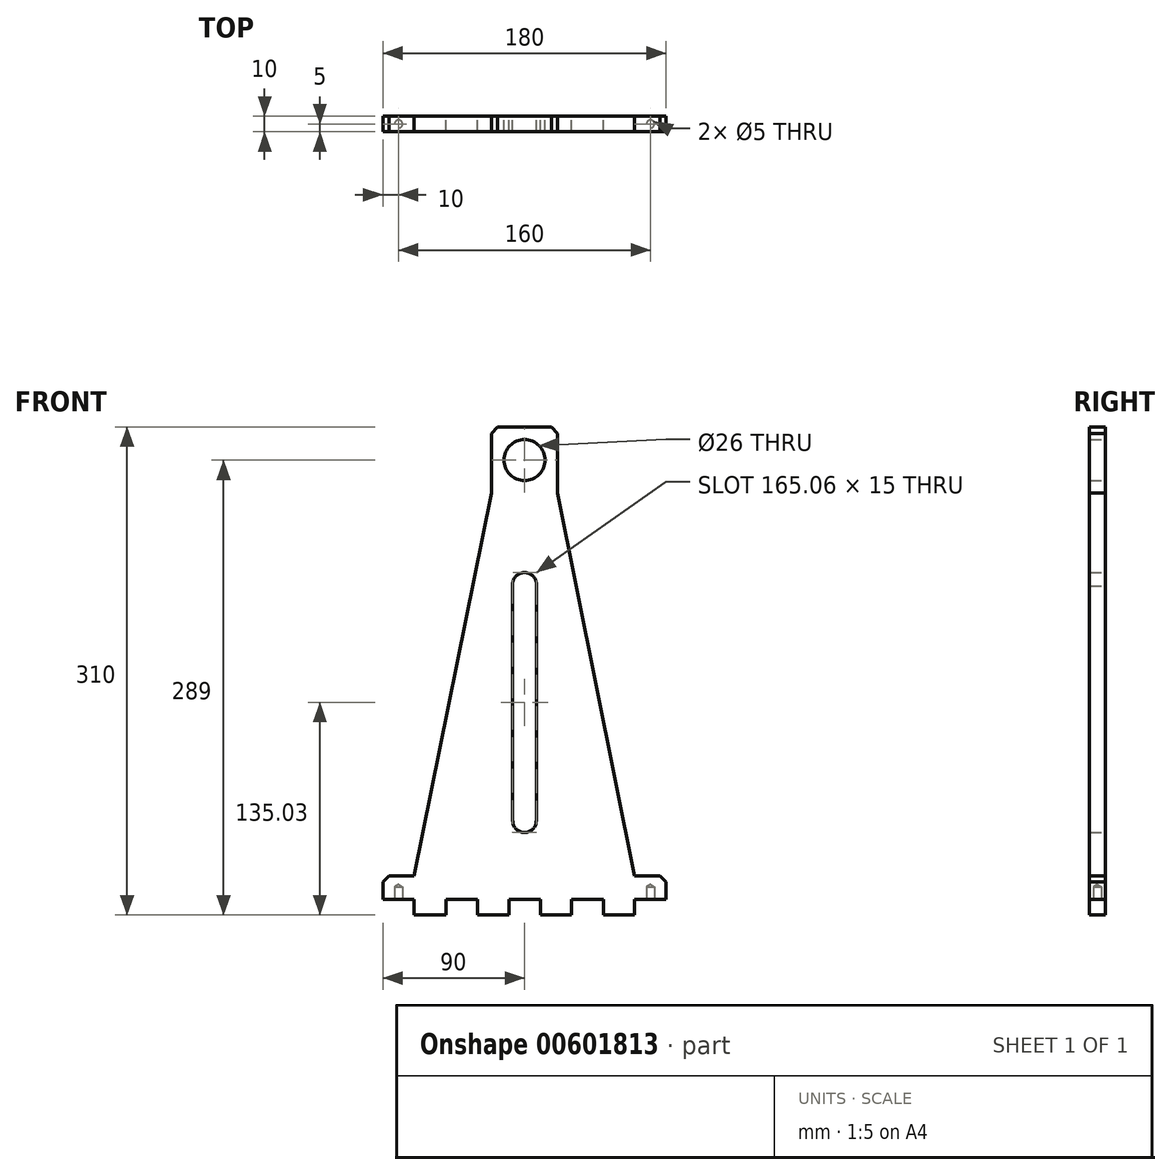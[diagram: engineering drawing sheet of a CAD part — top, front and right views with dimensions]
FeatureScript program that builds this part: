
annotation { "Feature Type Name" : "Feature", "Feature Type Description" : "" }
export const myFeature = defineFeature(function(context is Context, id is Id, definition is map)
    precondition{}
    {
        {
            var Q0;
            Q0=qCreatedBy(makeId("Front.planeOp"),FACE);
            var sketch = newSketch(context, id + "F0", { "sketchPlane" : qUnion([Q0])});
            skLineSegment(sketch, "E0.bottom", {"start": v(0, 0) * mm, "end": v(-10, 0) * mm});
            skLineSegment(sketch, "E0.left", {"start": v(0, 0) * mm, "end": v(0, 300) * mm, "construction": true});
            skLineSegment(sketch, "E1", {"start": v(-90, 0) * mm, "end": v(-90, 15) * mm});
            skLineSegment(sketch, "E2", {"start": v(-90, 15) * mm, "end": v(-70, 15) * mm});
            skLineSegment(sketch, "E3", {"start": v(-70, 15) * mm, "end": v(-21, 258) * mm});
            skLineSegment(sketch, "E4", {"start": v(-21, 258) * mm, "end": v(-21, 300) * mm});
            skLineSegment(sketch, "E5", {"start": v(-21, 300) * mm, "end": v(0, 300) * mm});
            skLineSegment(sketch, "E6", {"start": v(-21, 279) * mm, "end": v(0, 279) * mm, "construction": true});
            skLineSegment(sketch, "E7.bottom", {"start": v(15.5, 294.5) * mm, "end": v(-15.5, 294.5) * mm, "construction": true});
            skLineSegment(sketch, "E7.top", {"start": v(15.5, 263.5) * mm, "end": v(-15.5, 263.5) * mm, "construction": true});
            skLineSegment(sketch, "E7.left", {"start": v(15.5, 294.5) * mm, "end": v(15.5, 263.5) * mm, "construction": true});
            skLineSegment(sketch, "E7.right", {"start": v(-15.5, 294.5) * mm, "end": v(-15.5, 263.5) * mm, "construction": true});
            skPoint(sketch, "E7.middle", {"position": v(0, 279) * mm});
            skArc(sketch, "E8", {"start": v(-7.5, 50) * mm, "mid": v(0, 42.5) * mm, "end": v(7.5, 50) * mm});
            skArc(sketch, "E9", {"start": v(7.5, 199.05) * mm, "mid": v(0, 207.56) * mm, "end": v(-7.5, 199.05) * mm});
            skLineSegment(sketch, "E10", {"start": v(7.5, 50) * mm, "end": v(7.5, 199.05) * mm});
            skLineSegment(sketch, "E11.MirrorCS", {"start": v(-7.5, 50) * mm, "end": v(-7.5, 199.05) * mm});
            skLineSegment(sketch, "E12.MirrorCS", {"start": v(0, 0) * mm, "end": v(10, 0) * mm});
            skLineSegment(sketch, "E13.MirrorCS", {"start": v(90, 0) * mm, "end": v(90, 15) * mm});
            skLineSegment(sketch, "E14.MirrorCS", {"start": v(90, 15) * mm, "end": v(70, 15) * mm});
            skLineSegment(sketch, "E15.MirrorCS", {"start": v(70, 15) * mm, "end": v(21, 258) * mm});
            skLineSegment(sketch, "E16.MirrorCS", {"start": v(21, 258) * mm, "end": v(21, 300) * mm});
            skLineSegment(sketch, "E17.MirrorCS", {"start": v(21, 300) * mm, "end": v(0, 300) * mm});
            skCircle(sketch, "E18", {"center": v(0, 279) * mm, "radius": 13 * mm});
            skLineSegment(sketch, "E19", {"start": v(-70, 0) * mm, "end": v(-70, -10) * mm});
            skLineSegment(sketch, "E20", {"start": v(-70, -10) * mm, "end": v(-50, -10) * mm});
            skLineSegment(sketch, "E21", {"start": v(-50, -10) * mm, "end": v(-50, 0) * mm});
            skLineSegment(sketch, "E22", {"start": v(-30, 0) * mm, "end": v(-30, -10) * mm});
            skLineSegment(sketch, "E23", {"start": v(-30, -10) * mm, "end": v(-10, -10) * mm});
            skLineSegment(sketch, "E24", {"start": v(-10, -10) * mm, "end": v(-10, 0) * mm});
            skLineSegment(sketch, "E25.MirrorCS", {"start": v(70, 0) * mm, "end": v(70, -10) * mm});
            skLineSegment(sketch, "E26.MirrorCS", {"start": v(70, -10) * mm, "end": v(50, -10) * mm});
            skLineSegment(sketch, "E27.MirrorCS", {"start": v(50, -10) * mm, "end": v(50, 0) * mm});
            skLineSegment(sketch, "E28.MirrorCS", {"start": v(30, 0) * mm, "end": v(30, -10) * mm});
            skLineSegment(sketch, "E29.MirrorCS", {"start": v(30, -10) * mm, "end": v(10, -10) * mm});
            skLineSegment(sketch, "E30.MirrorCS", {"start": v(10, -10) * mm, "end": v(10, 0) * mm});
            skLineSegment(sketch, "E31.trimOffspring", {"start": v(-70, 0) * mm, "end": v(-90, 0) * mm});
            skLineSegment(sketch, "E32.trimOffspring", {"start": v(-30, 0) * mm, "end": v(-50, 0) * mm});
            skLineSegment(sketch, "E33.trimOffspring", {"start": v(30, 0) * mm, "end": v(50, 0) * mm});
            skLineSegment(sketch, "E34.trimOffspring", {"start": v(70, 0) * mm, "end": v(90, 0) * mm});
            skSolve(sketch);
        }
        {
            var Q0;
            Q0=makeQuery(id+"F0.imprint","IMPRINT",FACE,{"disambiguationData":[TD([[makeQuery(id+"F0.imprint","IMPRINT",EDGE,{"derivedFrom":sQuery(id+"F0.wireOp",EDGE,"E0.bottom")}),-1.0]])]});
            extrude(context, id + "F1", {"entities" : qUnion([Q0]), "depth" : 10 * mm, "offsetDistance" : 25 * mm});
        }
        {
            var Q0;
            Q0=makeQuery(id+"F1.opExtrude","SWEPT_EDGE",EDGE,{"disambiguationData":[OSD([sQuery(id+"F0.wireOp",EDGE,"E16.MirrorCS"),sQuery(id+"F0.wireOp",EDGE,"E17.MirrorCS")])]});
            var Q1;
            Q1=makeQuery(id+"F1.opExtrude","SWEPT_EDGE",EDGE,{"disambiguationData":[OSD([sQuery(id+"F0.wireOp",EDGE,"E4"),sQuery(id+"F0.wireOp",EDGE,"E5")])]});
            chamfer(context, id + "F2", {"entities" : qUnion([Q0, Q1]), "width" : 4 * mm, "tangentPropagation" : true});
        }
        {
            var Q0;
            Q0=makeQuery(id+"F1.opExtrude","SWEPT_EDGE",EDGE,{"disambiguationData":[OSD([sQuery(id+"F0.wireOp",EDGE,"E1"),sQuery(id+"F0.wireOp",EDGE,"E2")])]});
            var Q1;
            Q1=makeQuery(id+"F1.opExtrude","SWEPT_EDGE",EDGE,{"disambiguationData":[OSD([sQuery(id+"F0.wireOp",EDGE,"E13.MirrorCS"),sQuery(id+"F0.wireOp",EDGE,"E14.MirrorCS")])]});
            chamfer(context, id + "F3", {"entities" : qUnion([Q0, Q1]), "width" : 4 * mm, "tangentPropagation" : true});
        }
        {
            var Q0;
            Q0=makeQuery(id+"F1.opExtrude","SWEPT_FACE",FACE,{"disambiguationData":[OSD([sQuery(id+"F0.wireOp",EDGE,"E31.trimOffspring")])]});
            var sketch = newSketch(context, id + "F4", { "sketchPlane" : qUnion([Q0])});
            skPoint(sketch, "E35", {"position": v(-80, 5) * mm});
            skPoint(sketch, "E35.positionSnap0", {"position": v(-90, 5) * mm});
            skPoint(sketch, "E36", {"position": v(80, 5) * mm});
            skSolve(sketch);
        }
        {
            var Q0;
            Q0=sQuery(id+"F4.wireOp",VERTEX,"E35");
            var Q1;
            Q1=sQuery(id+"F4.wireOp",VERTEX,"E36");
            var Q2;
            Q2=makeQuery(id+"F1.opExtrude","SWEPT_BODY",BODY,{"disambiguationData":[OSD([sQuery(id+"F0.wireOp",EDGE,"E0.bottom"),sQuery(id+"F0.wireOp",EDGE,"E1"),sQuery(id+"F0.wireOp",EDGE,"E2"),sQuery(id+"F0.wireOp",EDGE,"E3"),sQuery(id+"F0.wireOp",EDGE,"E4"),sQuery(id+"F0.wireOp",EDGE,"E5"),sQuery(id+"F0.wireOp",EDGE,"E8"),sQuery(id+"F0.wireOp",EDGE,"E9"),sQuery(id+"F0.wireOp",EDGE,"E10"),sQuery(id+"F0.wireOp",EDGE,"E11.MirrorCS"),sQuery(id+"F0.wireOp",EDGE,"E12.MirrorCS"),sQuery(id+"F0.wireOp",EDGE,"E13.MirrorCS"),sQuery(id+"F0.wireOp",EDGE,"E14.MirrorCS"),sQuery(id+"F0.wireOp",EDGE,"E15.MirrorCS"),sQuery(id+"F0.wireOp",EDGE,"E16.MirrorCS"),sQuery(id+"F0.wireOp",EDGE,"E17.MirrorCS"),sQuery(id+"F0.wireOp",EDGE,"E18"),sQuery(id+"F0.wireOp",EDGE,"E19"),sQuery(id+"F0.wireOp",EDGE,"E20"),sQuery(id+"F0.wireOp",EDGE,"E21"),sQuery(id+"F0.wireOp",EDGE,"E22"),sQuery(id+"F0.wireOp",EDGE,"E23"),sQuery(id+"F0.wireOp",EDGE,"E24"),sQuery(id+"F0.wireOp",EDGE,"E25.MirrorCS"),sQuery(id+"F0.wireOp",EDGE,"E26.MirrorCS"),sQuery(id+"F0.wireOp",EDGE,"E27.MirrorCS"),sQuery(id+"F0.wireOp",EDGE,"E28.MirrorCS"),sQuery(id+"F0.wireOp",EDGE,"E29.MirrorCS"),sQuery(id+"F0.wireOp",EDGE,"E30.MirrorCS"),sQuery(id+"F0.wireOp",EDGE,"E31.trimOffspring"),sQuery(id+"F0.wireOp",EDGE,"E32.trimOffspring"),sQuery(id+"F0.wireOp",EDGE,"E33.trimOffspring"),sQuery(id+"F0.wireOp",EDGE,"E34.trimOffspring")])]});
            hole(context, id + "F5", {"style" : HoleStyle.SIMPLE, "endStyle" : HoleEndStyle.BLIND, "standardTappedOrClearance" : lookupTablePath({ "standard" : "ISO", "engagement" : "75%", "pitch" : "1 mm", "size" : "M6", "type" : "Tapped" }), "standardBlindInLast" : lookupTablePath({ "standard" : "ISO", "engagement" : "75%", "pitch" : "1 mm", "size" : "M6", "type" : "Tapped" }), "holeDiameter" : 5 * mm, "majorDiameter" : 6 * mm, "showTappedDepth" : true, "holeDepth" : 8 * mm, "isTappedThrough" : true, "tappedDepth" : 5 * mm, "tapClearance" : 3, "locations" : qUnion([Q0, Q1]), "scope" : qUnion([Q2])});
        }
    });
